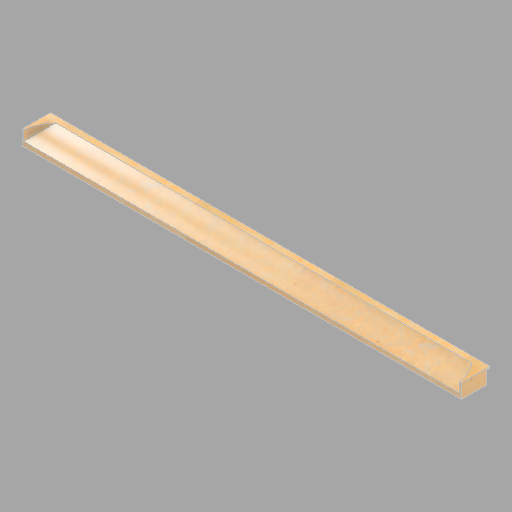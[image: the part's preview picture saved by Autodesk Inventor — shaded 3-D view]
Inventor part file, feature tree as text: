
AUTODESK INVENTOR PART (.ipt)
format: ipt  version: 2022.2 (Build 262287010, 287A)  size: 172,032 bytes
history: native  units: in
note: dims shown in document units (in); Inventor stores cm internally (conversion verified against a paired STEP export)
features: revolve x2, direct_edit x1
ambient origin geometry x8: Origin, YZ Plane, XZ Plane, XY Plane, X Axis, Y Axis, Z Axis, Center Point
bodies: Solid1 (feature_tree), Body1 (feature_tree)
feature tree (3):
  direct_edit  "Direct Edit1"
  revolve  "Rotate1"  Angle=180.0deg
  revolve  "Rotate2"  [1 undecoded]
note: 1 required parameter value undecoded (feature->parameter linkage not recoverable at this tier; creation-order binding heuristic only, values carry confidence <= 0.55)
